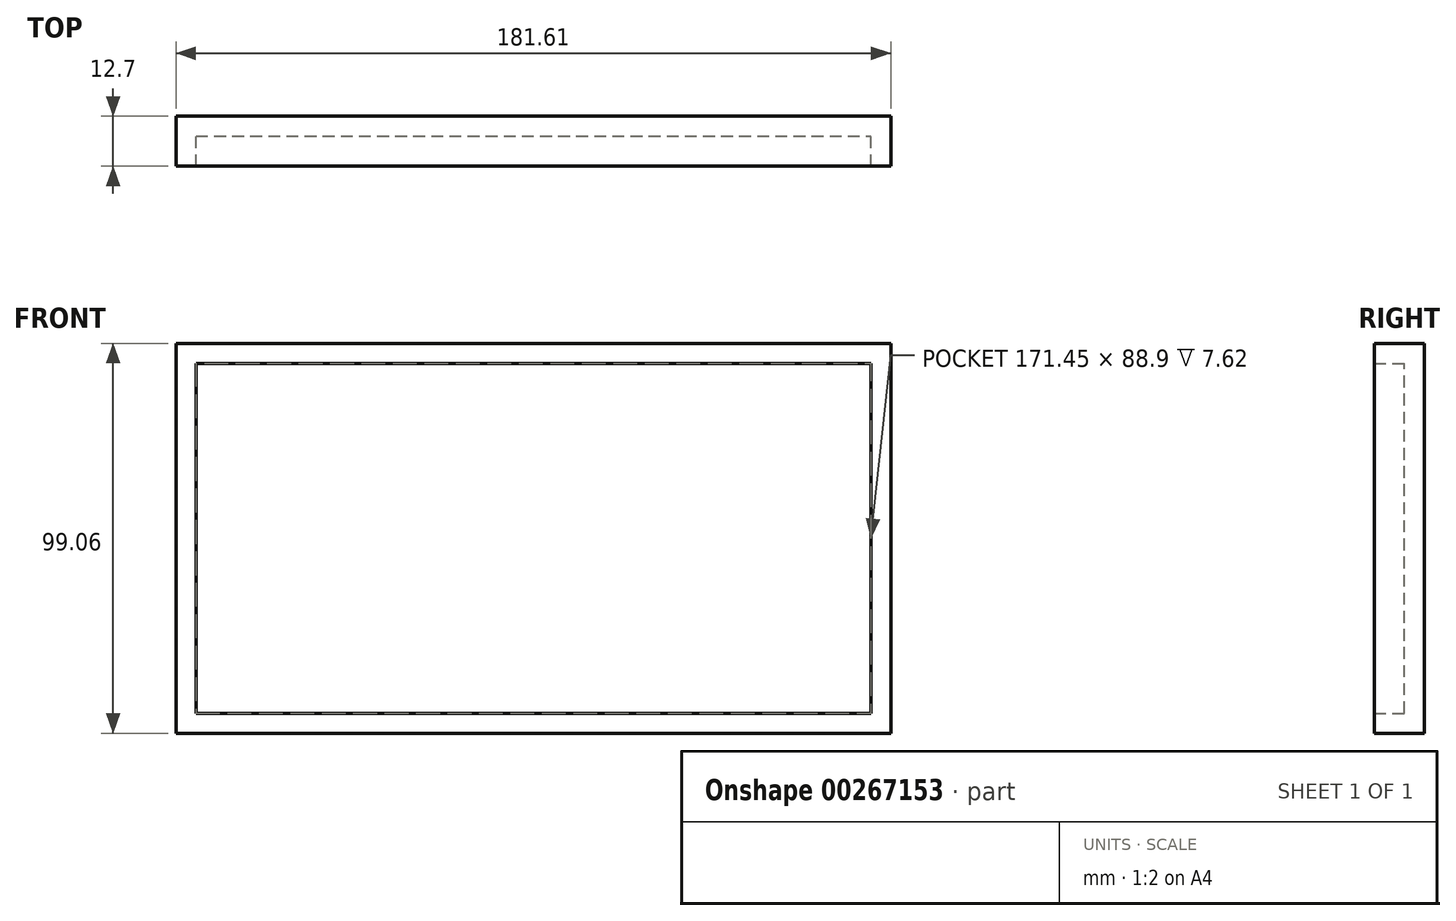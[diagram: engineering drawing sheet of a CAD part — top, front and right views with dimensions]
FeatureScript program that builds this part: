
annotation { "Feature Type Name" : "Feature", "Feature Type Description" : "" }
export const myFeature = defineFeature(function(context is Context, id is Id, definition is map)
    precondition{}
    {
        {
            var Q0;
            Q0=qCreatedBy(makeId("Front.planeOp"),FACE);
            var sketch = newSketch(context, id + "F0", { "sketchPlane" : qUnion([Q0])});
            skLineSegment(sketch, "E0.bottom", {"start": v(0, 0) * mm, "end": v(171.45, 0) * mm});
            skLineSegment(sketch, "E0.top", {"start": v(0, 88.9) * mm, "end": v(171.45, 88.9) * mm});
            skLineSegment(sketch, "E0.left", {"start": v(0, 0) * mm, "end": v(0, 88.9) * mm});
            skLineSegment(sketch, "E0.right", {"start": v(171.45, 0) * mm, "end": v(171.45, 88.9) * mm});
            skLineSegment(sketch, "E1.top", {"start": v(0, -5.08) * mm, "end": v(171.45, -5.08) * mm});
            skLineSegment(sketch, "E1.left", {"start": v(0, 0) * mm, "end": v(0, -5.08) * mm});
            skLineSegment(sketch, "E1.right", {"start": v(171.45, 0) * mm, "end": v(171.45, -5.08) * mm});
            skLineSegment(sketch, "E2.bottom", {"start": v(171.45, -5.08) * mm, "end": v(176.53, -5.08) * mm});
            skLineSegment(sketch, "E2.top", {"start": v(171.45, 88.9) * mm, "end": v(176.53, 88.9) * mm});
            skLineSegment(sketch, "E2.left", {"start": v(171.45, -5.08) * mm, "end": v(171.45, 88.9) * mm});
            skLineSegment(sketch, "E2.right", {"start": v(176.53, -5.08) * mm, "end": v(176.53, 88.9) * mm});
            skLineSegment(sketch, "E3.bottom", {"start": v(176.53, 88.9) * mm, "end": v(0, 88.9) * mm});
            skLineSegment(sketch, "E3.top", {"start": v(176.53, 93.98) * mm, "end": v(0, 93.98) * mm});
            skLineSegment(sketch, "E3.left", {"start": v(176.53, 88.9) * mm, "end": v(176.53, 93.98) * mm});
            skLineSegment(sketch, "E3.right", {"start": v(0, 88.9) * mm, "end": v(0, 93.98) * mm});
            skLineSegment(sketch, "E4.bottom", {"start": v(0, 93.98) * mm, "end": v(-5.08, 93.98) * mm});
            skLineSegment(sketch, "E4.top", {"start": v(0, -5.08) * mm, "end": v(-5.08, -5.08) * mm});
            skLineSegment(sketch, "E4.left", {"start": v(0, 93.98) * mm, "end": v(0, -5.08) * mm});
            skLineSegment(sketch, "E4.right", {"start": v(-5.08, 93.98) * mm, "end": v(-5.08, -5.08) * mm});
            skSolve(sketch);
        }
        {
            var Q0;
            Q0 = qSketchRegion(id + "F0", true);
            extrude(context, id + "F1", {"entities" : qUnion([Q0]), "depth" : 12.7 * mm});
        }
        {
            var Q0;
            {var subQ0=sQuery(id+"F0.wireOp",EDGE,"E0.bottom");Q0=makeQuery(id+"F0.imprint","IMPRINT",FACE,{"disambiguationData":[TD([[makeQuery(id+"F0.imprint","IMPRINT",EDGE,{"derivedFrom":subQ0}),1.0]])]});}
            extrude(context, id + "F2", {"entities" : qUnion([Q0]), "operationType" : NewBodyOperationType.ADD, "depth" : 5.08 * mm});
        }
    });
